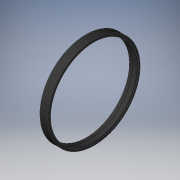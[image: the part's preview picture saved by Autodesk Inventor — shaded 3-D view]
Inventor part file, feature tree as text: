
AUTODESK INVENTOR PART (.ipt)
format: ipt  version: 2019 (Build 230136000, 136)  size: 192,512 bytes
history: native  units: mm
features: other x7, revolve x1, sketch x1
ambient origin geometry x8: Origin, YZ Plane, XZ Plane, XY Plane, X Axis, Y Axis, Z Axis, Center Point
bodies: Solid1 (feature_tree)
feature tree (9):
  revolve  "Revolution1"  [1 undecoded]
  other  "or_XY"
  other  "or_YZ"
  other  "or_ZX"
  other  "or_X"
  other  "or_Y"
  other  "or_Z"
  other  "or_Center"
  sketch  "Sketch_15"  dims[d0=360.0deg]
note: 1 required parameter value undecoded (feature->parameter linkage not recoverable at this tier; creation-order binding heuristic only, values carry confidence <= 0.55)
